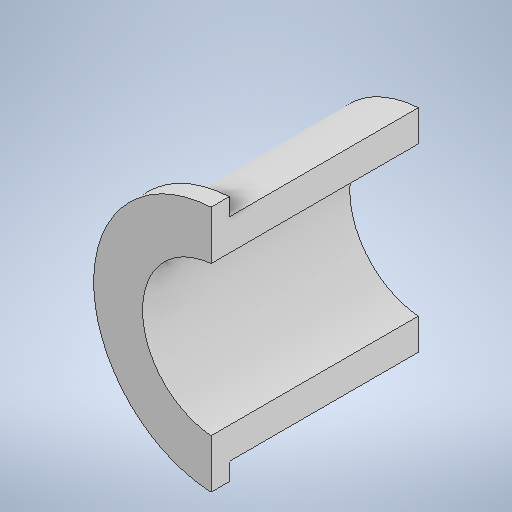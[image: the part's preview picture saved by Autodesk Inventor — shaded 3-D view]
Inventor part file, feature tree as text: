
AUTODESK INVENTOR PART (.ipt)
format: ipt  version: 2025 (Build 290162000, 162)  size: 229,888 bytes
history: native  units: in
note: dims shown in document units (in); Inventor stores cm internally (conversion verified against a paired STEP export)
features: extrude x2, sketch x2
ambient origin geometry x8: Origin, YZ Plane, XZ Plane, XY Plane, X Axis, Y Axis, Z Axis, Center Point
bodies: Solid1 (feature_tree)
feature tree (4):
  extrude  "Extrusion1"  TaperAngle=90.0deg  [1 undecoded]
  extrude  "Extrusion2"  Depth=0.5965in
  sketch  "Sketch1"  dims[d0=0.8413in d1=90.0deg]
  sketch  "Sketch2"  dims[d2=0.0354in d3=0.5965in d4=1.063in d5=0.0in d6=0.6949in d7=0.1024in d8=0.0in]
note: 1 required parameter value undecoded (feature->parameter linkage not recoverable at this tier; creation-order binding heuristic only, values carry confidence <= 0.55)
